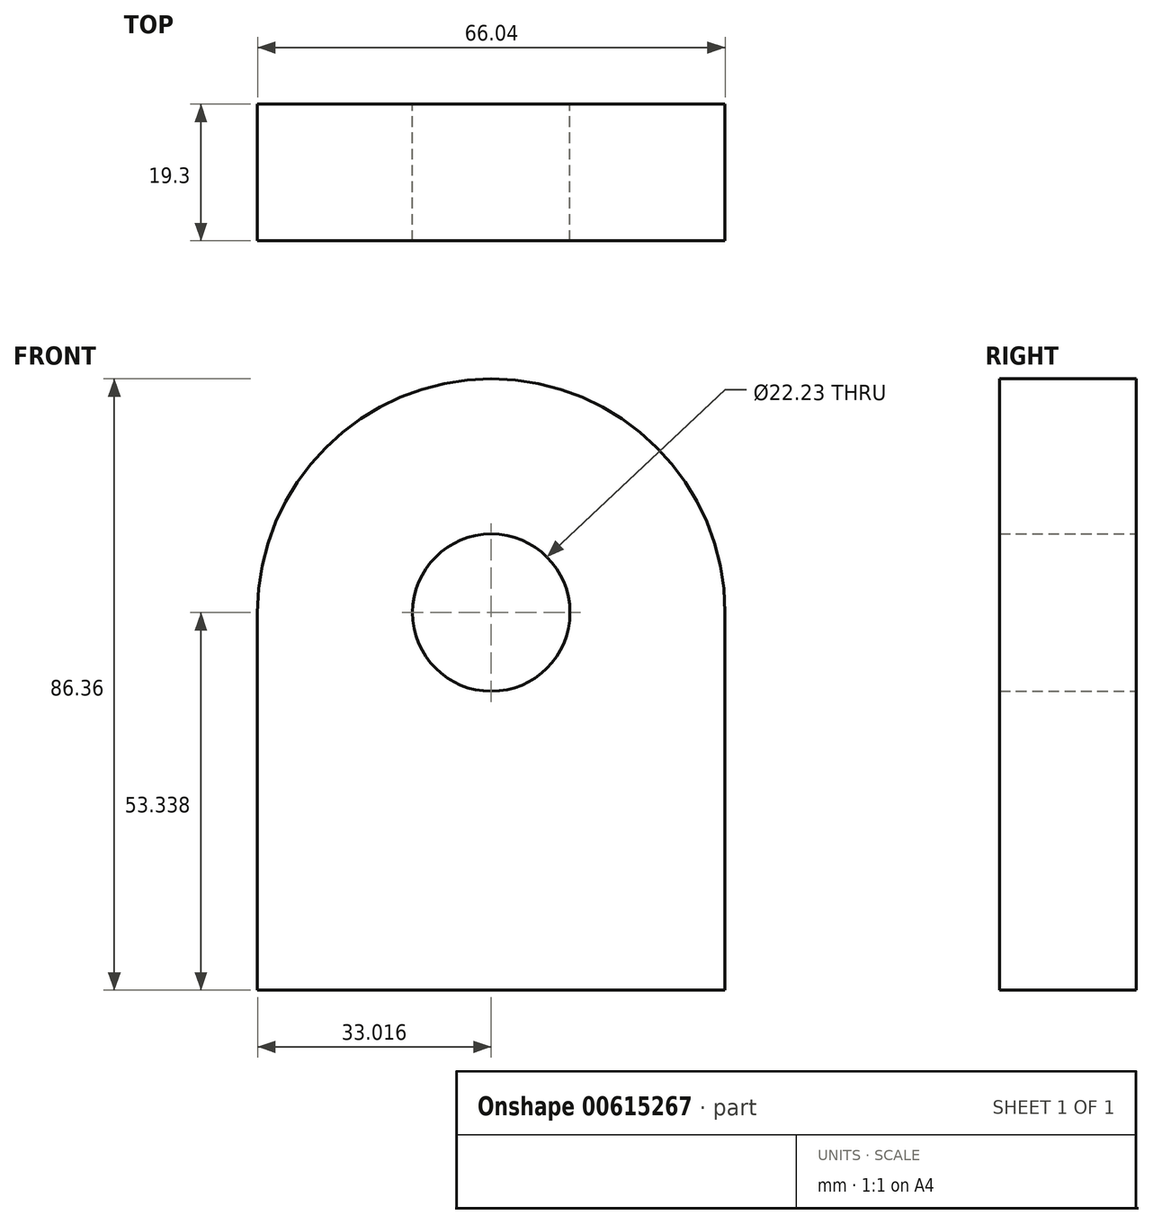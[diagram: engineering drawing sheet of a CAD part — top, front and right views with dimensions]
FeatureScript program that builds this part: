
annotation { "Feature Type Name" : "Feature", "Feature Type Description" : "" }
export const myFeature = defineFeature(function(context is Context, id is Id, definition is map)
    precondition{}
    {
        {
            var Q0;
            Q0=qCreatedBy(makeId("Front.planeOp"),FACE);
            var sketch = newSketch(context, id + "F0", { "sketchPlane" : qUnion([Q0])});
            skLineSegment(sketch, "E0.bottom", {"start": v(23.98, 35.76) * mm, "end": v(23.98, 35.76) * mm});
            skLineSegment(sketch, "E0.top", {"start": v(-9.04, -50.6) * mm, "end": v(57, -50.6) * mm});
            skLineSegment(sketch, "E0.left", {"start": v(-9.04, 2.74) * mm, "end": v(-9.04, -50.6) * mm});
            skLineSegment(sketch, "E0.right", {"start": v(57, 2.74) * mm, "end": v(57, -50.6) * mm});
            skPoint(sketch, "E1.visualSharp", {"position": v(-9.04, 35.76) * mm});
            skArc(sketch, "E1.filletArc", {"start": v(23.98, 35.76) * mm, "mid": v(0.63, 26.09) * mm, "end": v(-9.04, 2.74) * mm});
            skPoint(sketch, "E2.visualSharp", {"position": v(57, 35.76) * mm});
            skArc(sketch, "E2.filletArc", {"start": v(57, 2.74) * mm, "mid": v(47.32, 26.09) * mm, "end": v(23.98, 35.76) * mm});
            skCircle(sketch, "E3", {"center": v(23.98, 2.74) * mm, "radius": 11.11 * mm});
            skSolve(sketch);
        }
        {
            var Q0;
            Q0 = qSketchRegion(id + "F0", true);
            extrude(context, id + "F1", {"entities" : qUnion([Q0]), "depth" : 19.3 * mm, "offsetDistance" : 25.4 * mm});
        }
    });
